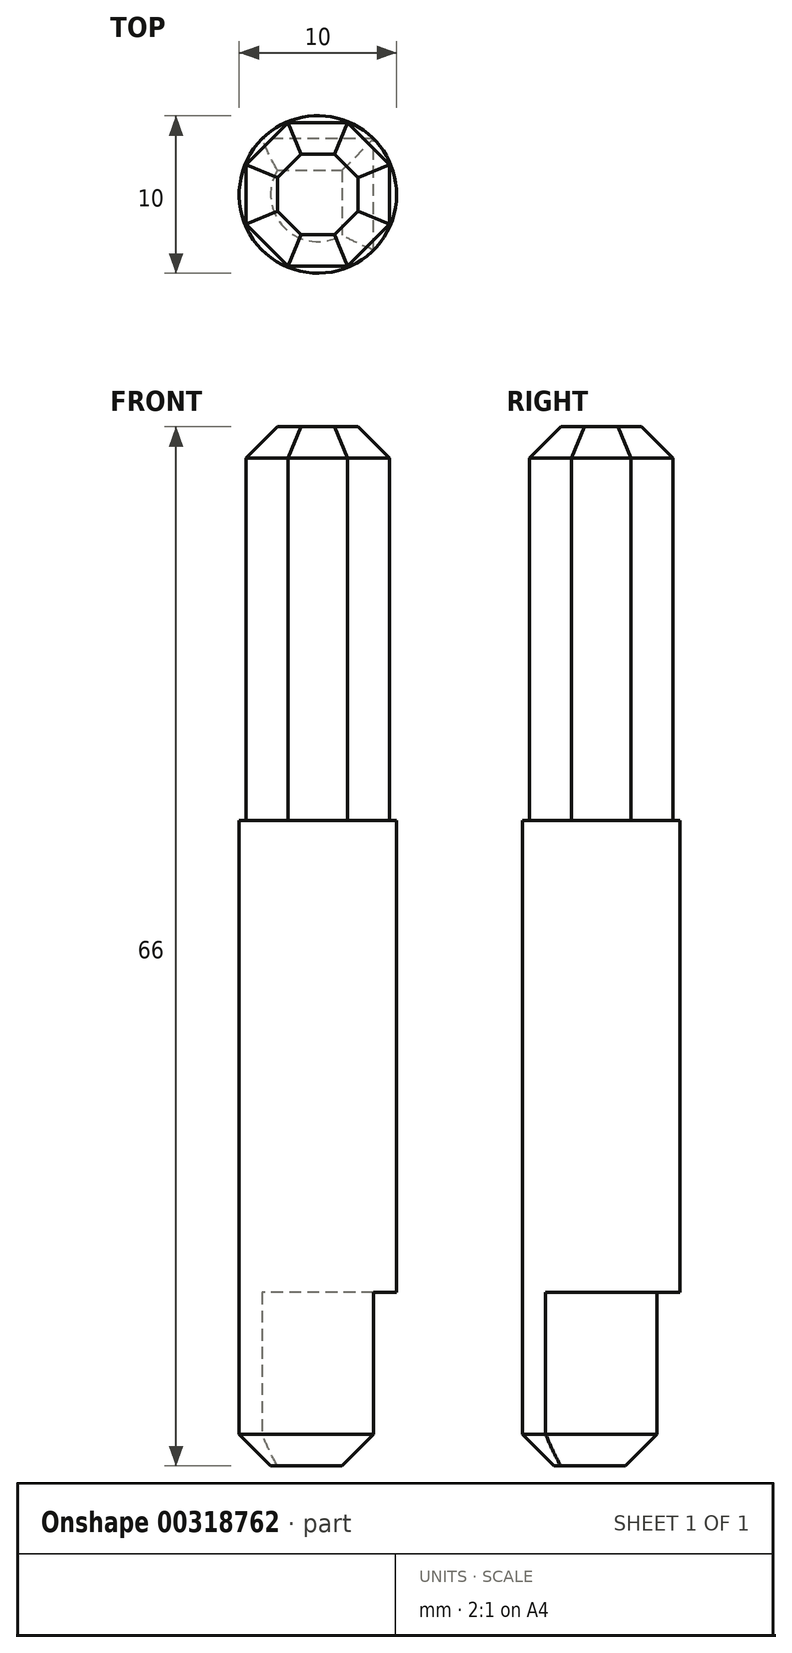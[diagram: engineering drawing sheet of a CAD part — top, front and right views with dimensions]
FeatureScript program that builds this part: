
annotation { "Feature Type Name" : "Feature", "Feature Type Description" : "" }
export const myFeature = defineFeature(function(context is Context, id is Id, definition is map)
    precondition{}
    {
        {
            var Q0;
            Q0=qCreatedBy(makeId("Top.planeOp"),FACE);
            var sketch = newSketch(context, id + "F0", { "sketchPlane" : qUnion([Q0])});
            skCircle(sketch, "E0", {"center": v(0, 0) * mm, "radius": 5 * mm});
            skSolve(sketch);
        }
        {
            var Q0;
            Q0=makeQuery(id+"F0.imprint","IMPRINT",FACE,{"disambiguationData":[TD([[makeQuery(id+"F0.imprint","IMPRINT",EDGE,{"derivedFrom":sQuery(id+"F0.wireOp",EDGE,"E0")}),1.0]])]});
            extrude(context, id + "F1", {"entities" : qUnion([Q0]), "depth" : 66 * mm, "offsetDistance" : 25 * mm});
        }
        {
            var Q0;
            Q0=makeQuery(id+"F1.opExtrude","CAP_FACE",FACE,{"disambiguationData":[OSD([sQuery(id+"F0.wireOp",EDGE,"E0")])],"isStart":false});
            var sketch = newSketch(context, id + "F2", { "sketchPlane" : qUnion([Q0])});
            skCircle(sketch, "E1.cCircle", {"center": v(0, 0) * mm, "radius": 4.92 * mm, "construction": true});
            skLineSegment(sketch, "E1.0", {"start": v(4.55, -1.88) * mm, "end": v(1.88, -4.55) * mm});
            skLineSegment(sketch, "E1.1", {"start": v(1.88, -4.55) * mm, "end": v(-1.88, -4.55) * mm});
            skLineSegment(sketch, "E1.2", {"start": v(-1.88, -4.55) * mm, "end": v(-4.55, -1.88) * mm});
            skLineSegment(sketch, "E1.3", {"start": v(-4.55, -1.88) * mm, "end": v(-4.55, 1.88) * mm});
            skLineSegment(sketch, "E1.4", {"start": v(-4.55, 1.88) * mm, "end": v(-1.88, 4.55) * mm});
            skLineSegment(sketch, "E1.5", {"start": v(-1.88, 4.55) * mm, "end": v(1.88, 4.55) * mm});
            skLineSegment(sketch, "E1.6", {"start": v(1.88, 4.55) * mm, "end": v(4.55, 1.88) * mm});
            skLineSegment(sketch, "E1.7", {"start": v(4.55, 1.88) * mm, "end": v(4.55, -1.88) * mm});
            skSolve(sketch);
        }
        {
            var Q0;
            Q0=makeQuery(id+"F2.imprint","IMPRINT",FACE,{"disambiguationData":[TD([[makeQuery(id+"F2.imprint","IMPRINT",EDGE,{"derivedFrom":sQuery(id+"F2.wireOp",EDGE,"E1.0")}),1.0]])]});
            extrude(context, id + "F3", {"entities" : qUnion([Q0]), "operationType" : NewBodyOperationType.REMOVE, "oppositeDirection" : true, "depth" : 25 * mm, "offsetDistance" : 25 * mm});
        }
        {
            var Q0;
            Q0=makeQuery(id+"F1.opExtrude","CAP_FACE",FACE,{"disambiguationData":[OSD([sQuery(id+"F0.wireOp",EDGE,"E0")])],"isStart":true});
            var sketch = newSketch(context, id + "F4", { "sketchPlane" : qUnion([Q0])});
            skLineSegment(sketch, "E2", {"start": v(3.54, 3.54) * mm, "end": v(3.54, -3.54) * mm});
            skLineSegment(sketch, "E3", {"start": v(3.54, -3.54) * mm, "end": v(-3.54, -3.54) * mm});
            skSolve(sketch);
        }
        {
            var Q0;
            {var subQ0=sQuery(id+"F4.wireOp",EDGE,"E2");Q0=makeQuery(id+"F4.imprint","IMPRINT",FACE,{"disambiguationData":[TD([[makeQuery(id+"F4.imprint","IMPRINT",EDGE,{"derivedFrom":subQ0}),1.0]])]});}
            var Q1;
            {var subQ0=sQuery(id+"F4.wireOp",EDGE,"E3");Q1=makeQuery(id+"F4.imprint","IMPRINT",FACE,{"disambiguationData":[TD([[makeQuery(id+"F4.imprint","IMPRINT",EDGE,{"derivedFrom":subQ0}),1.0]])]});}
            extrude(context, id + "F5", {"entities" : qUnion([Q0, Q1]), "operationType" : NewBodyOperationType.REMOVE, "oppositeDirection" : true, "depth" : 11 * mm, "offsetDistance" : 25 * mm});
        }
        {
            var Q0;
            Q0=makeQuery(id+"F1.opExtrude","CAP_FACE",FACE,{"disambiguationData":[OSD([sQuery(id+"F0.wireOp",EDGE,"E0")])],"isStart":false});
            var Q1;
            Q1=makeQuery(id+"F1.opExtrude","CAP_FACE",FACE,{"disambiguationData":[OSD([sQuery(id+"F0.wireOp",EDGE,"E0")])],"isStart":true});
            chamfer(context, id + "F6", {"entities" : qUnion([Q0, Q1]), "chamferType" : ChamferType.TWO_OFFSETS, "width1" : 2 * mm, "oppositeDirection" : false, "width2" : 2 * mm, "tangentPropagation" : true});
        }
    });
